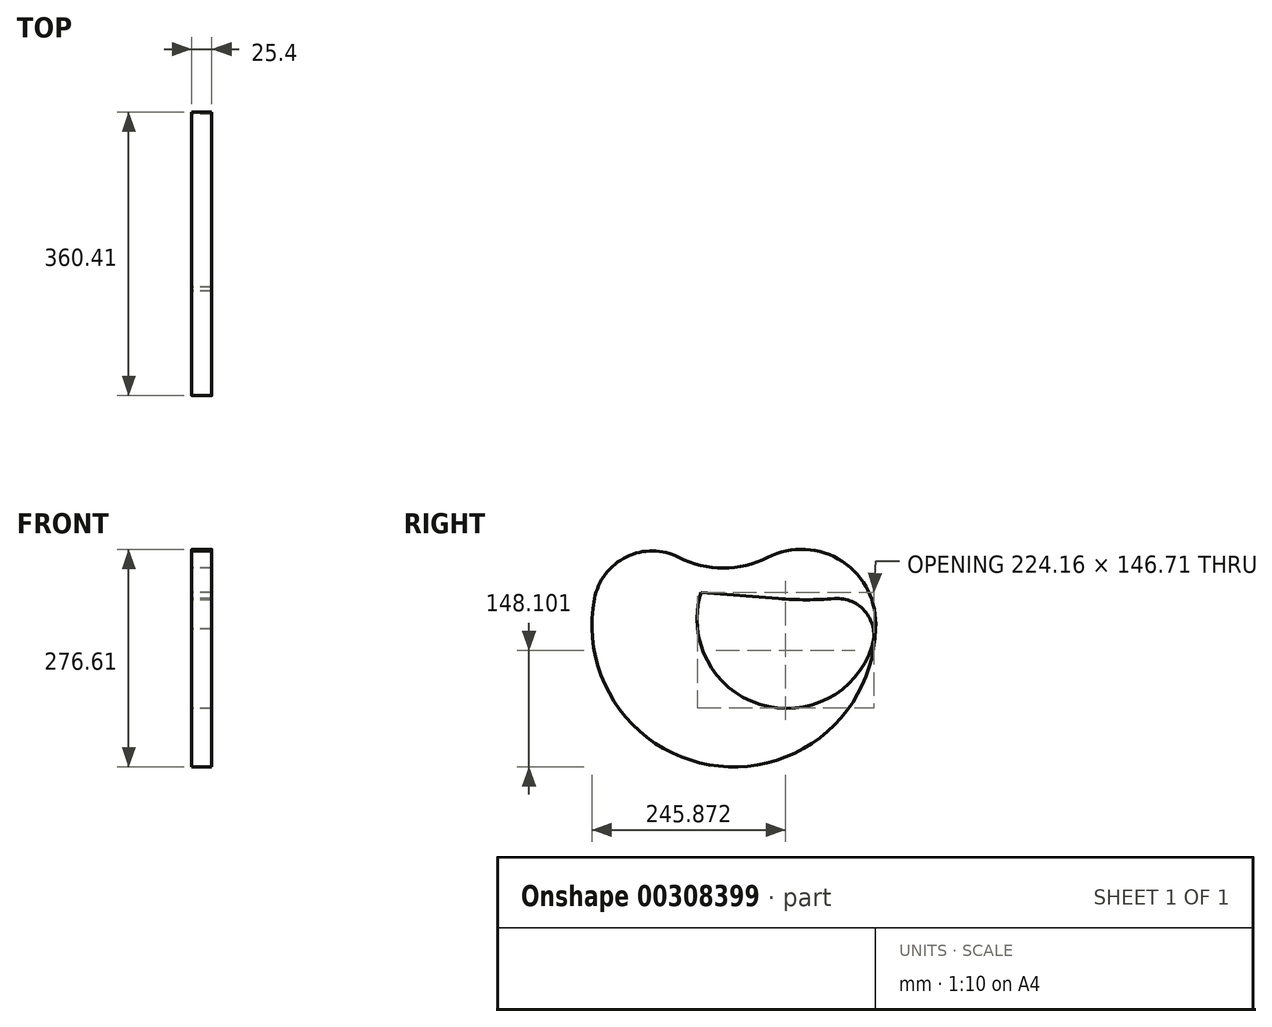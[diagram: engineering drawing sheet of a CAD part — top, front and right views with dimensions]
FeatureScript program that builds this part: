
annotation { "Feature Type Name" : "Feature", "Feature Type Description" : "" }
export const myFeature = defineFeature(function(context is Context, id is Id, definition is map)
    precondition{}
    {
        {
            var Q0;
            Q0=qCreatedBy(makeId("Right.planeOp"),FACE);
            var sketch = newSketch(context, id + "F0", { "sketchPlane" : qUnion([Q0])});
            skLineSegment(sketch, "E0", {"start": v(-84.93, -28.94) * mm, "end": v(13.8, -36.63) * mm});
            skArc(sketch, "E1", {"start": v(13.8, -36.63) * mm, "mid": v(49.36, -38.01) * mm, "end": v(84.93, -36.63) * mm});
            skArc(sketch, "E2", {"start": v(84.93, -36.63) * mm, "mid": v(125.02, -54.2) * mm, "end": v(132.7, -97.3) * mm});
            skArc(sketch, "E3", {"start": v(132.7, -97.3) * mm, "mid": v(-9.95, -170.83) * mm, "end": v(-84.93, -28.94) * mm});
            skArc(sketch, "E4", {"start": v(132.7, -97.3) * mm, "mid": v(104.2, 3.66) * mm, "end": v(0, 15.84) * mm});
            skArc(sketch, "E5", {"start": v(0, 15.84) * mm, "mid": v(-56.3, 2.26) * mm, "end": v(-112.62, 15.84) * mm});
            skArc(sketch, "E6", {"start": v(-112.62, 15.84) * mm, "mid": v(-179.4, 16.46) * mm, "end": v(-219.92, -36.63) * mm});
            skArc(sketch, "E7", {"start": v(-219.92, -36.63) * mm, "mid": v(-62.11, -249.38) * mm, "end": v(137.09, -74.78) * mm});
            skSolve(sketch);
        }
        {
            var Q0;
            Q0 = qSketchRegion(id + "F0", true);
            extrude(context, id + "F1", {"entities" : qUnion([Q0]), "depth" : 25.4 * mm});
        }
    });
